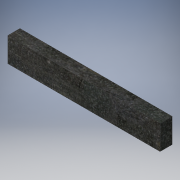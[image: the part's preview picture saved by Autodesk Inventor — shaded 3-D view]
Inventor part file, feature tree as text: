
AUTODESK INVENTOR PART (.ipt)
format: ipt  version: 2019 (Build 230136000, 136)  size: 110,080 bytes
history: native  units: mm
features: extrude x1, sketch x1
ambient origin geometry x8: Origin, YZ Plane, XZ Plane, XY Plane, X Axis, Y Axis, Z Axis, Center Point
bodies: Solid1 (feature_tree)
feature tree (2):
  extrude  "Extrusion1"  Depth=10.0mm
  sketch  "Sketch1"  dims[d0=125.0mm d1=20.0mm d6=267.645673mm d7=10.0mm d8=217.645673mm d9=10.0mm d10=10.0mm d11=0.0mm]
